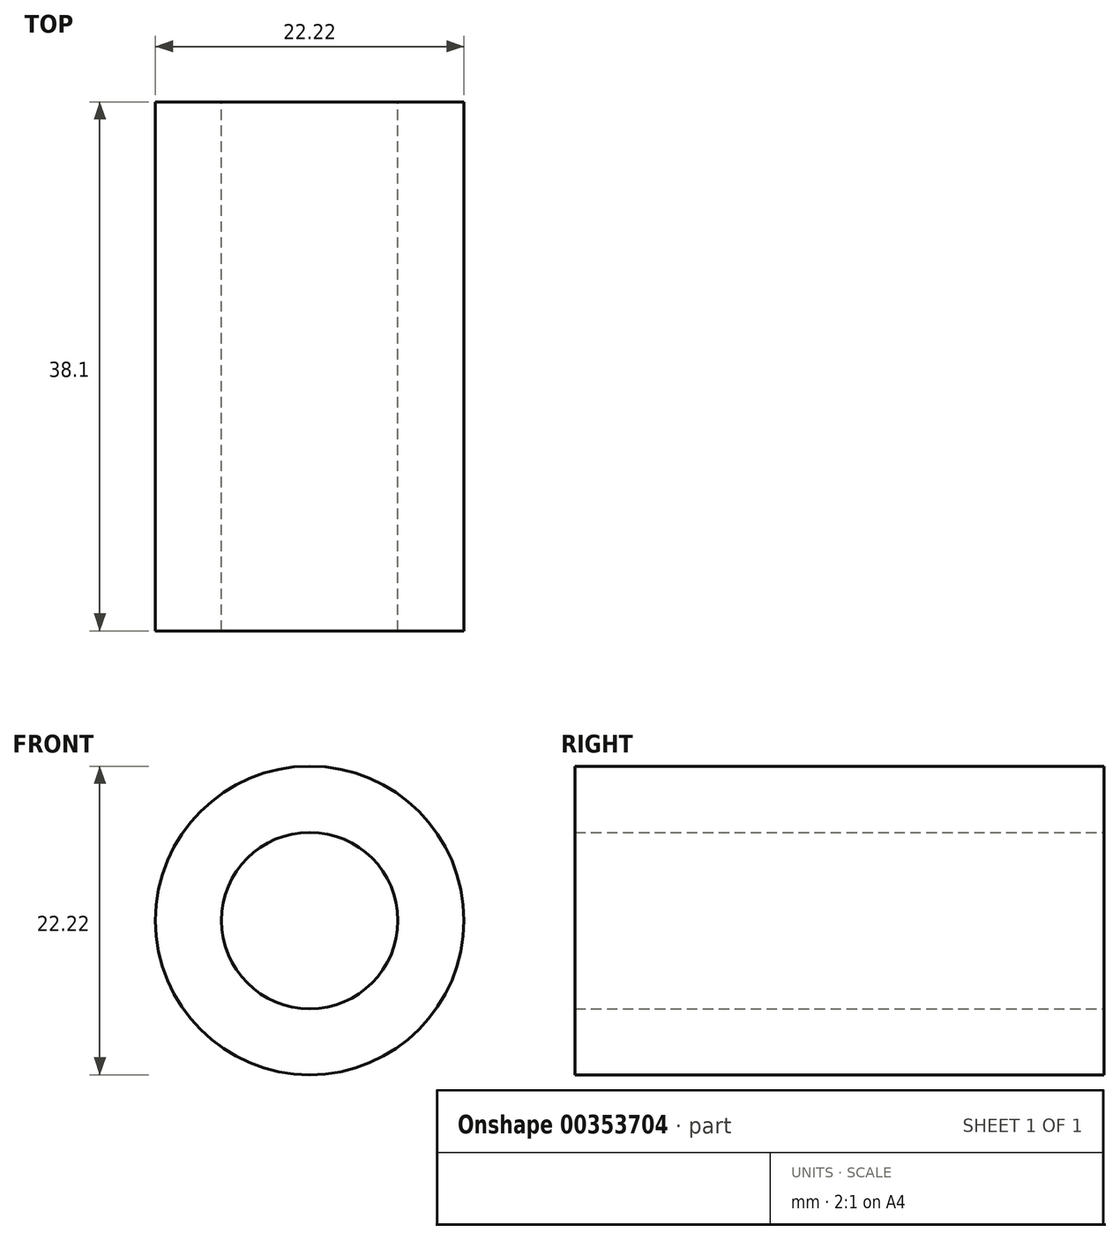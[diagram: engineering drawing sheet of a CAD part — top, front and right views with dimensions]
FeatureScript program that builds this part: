
annotation { "Feature Type Name" : "Feature", "Feature Type Description" : "" }
export const myFeature = defineFeature(function(context is Context, id is Id, definition is map)
    precondition{}
    {
        {
            var Q0;
            Q0=qCreatedBy(makeId("Front.planeOp"),FACE);
            var sketch = newSketch(context, id + "F0", { "sketchPlane" : qUnion([Q0])});
            skCircle(sketch, "E0", {"center": v(0, 0) * mm, "radius": 11.11 * mm});
            skSolve(sketch);
        }
        {
            var Q0;
            Q0 = qSketchRegion(id + "F0", true);
            extrude(context, id + "F1", {"entities" : qUnion([Q0]), "depth" : 38.1 * mm, "symmetric" : true});
        }
        {
            var Q0;
            Q0=makeQuery(id+"F1.opExtrude","CAP_FACE",FACE,{"disambiguationData":[OSD([sQuery(id+"F0.wireOp",EDGE,"E0")])],"isStart":true});
            var sketch = newSketch(context, id + "F2", { "sketchPlane" : qUnion([Q0])});
            skCircle(sketch, "E1", {"center": v(0, 0) * mm, "radius": 6.35 * mm});
            skSolve(sketch);
        }
        {
            var Q0;
            Q0 = qSketchRegion(id + "F2", true);
            extrude(context, id + "F3", {"entities" : qUnion([Q0]), "operationType" : NewBodyOperationType.REMOVE, "oppositeDirection" : true, "depth" : 38.1 * mm});
        }
    });
